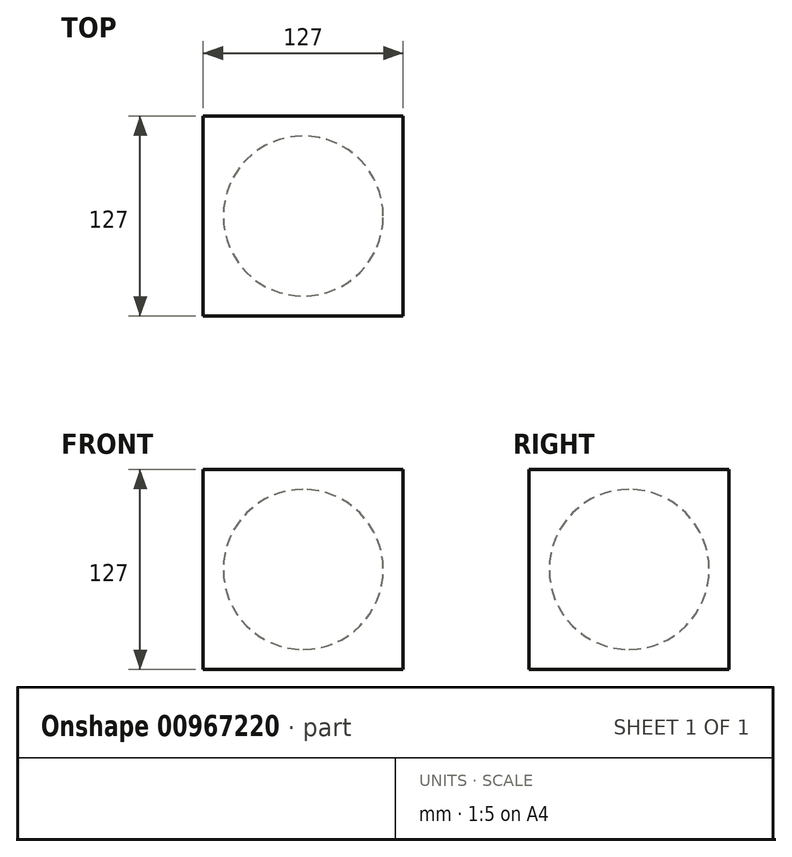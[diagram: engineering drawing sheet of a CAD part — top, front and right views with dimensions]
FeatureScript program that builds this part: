
annotation { "Feature Type Name" : "Feature", "Feature Type Description" : "" }
export const myFeature = defineFeature(function(context is Context, id is Id, definition is map)
    precondition{}
    {
        {
            var Q0;
            Q0=qCreatedBy(makeId("Front.planeOp"),FACE);
            var sketch = newSketch(context, id + "F0", { "sketchPlane" : qUnion([Q0])});
            skLineSegment(sketch, "E0.bottom", {"start": v(63.5, 63.5) * mm, "end": v(-63.5, 63.5) * mm});
            skLineSegment(sketch, "E0.top", {"start": v(63.5, -63.5) * mm, "end": v(-63.5, -63.5) * mm});
            skLineSegment(sketch, "E0.left", {"start": v(63.5, 63.5) * mm, "end": v(63.5, -63.5) * mm});
            skLineSegment(sketch, "E0.right", {"start": v(-63.5, 63.5) * mm, "end": v(-63.5, -63.5) * mm});
            skPoint(sketch, "E0.middle", {"position": v(0, 0) * mm});
            skPoint(sketch, "E1", {"position": v(0, 50.8) * mm});
            skSolve(sketch);
        }
        {
            var Q0;
            Q0=qCreatedBy(makeId("Front.planeOp"),FACE);
            var sketch = newSketch(context, id + "F1", { "sketchPlane" : qUnion([Q0])});
            skArc(sketch, "E2", {"start": v(0, -50.8) * mm, "mid": v(50.8, 0) * mm, "end": v(0, 50.8) * mm});
            skLineSegment(sketch, "E3", {"start": v(0, -50.8) * mm, "end": v(0, 50.8) * mm});
            skSolve(sketch);
        }
        {
            var Q0;
            Q0=makeQuery(id+"F0.imprint","IMPRINT",FACE,{"disambiguationData":[TD([[makeQuery(id+"F0.imprint","IMPRINT",EDGE,{"derivedFrom":sQuery(id+"F0.wireOp",EDGE,"E0.bottom")}),1.0]])]});
            extrude(context, id + "F2", {"entities" : qUnion([Q0]), "endBound" : BoundingType.SYMMETRIC, "depth" : 127 * mm, "offsetDistance" : 25.4 * mm});
        }
        {
            var Q0;
            Q0 = qSketchRegion(id + "F1", true);
            var Q1;
            Q1=sQuery(id+"F1.wireOp",EDGE,"E3");
            revolve(context, id + "F3", {"operationType" : NewBodyOperationType.REMOVE, "surfaceOperationType" : NewSurfaceOperationType.NEW, "entities" : qUnion([Q0]), "axis" : qUnion([Q1]), "revolveType" : RevolveType.FULL});
        }
    });
